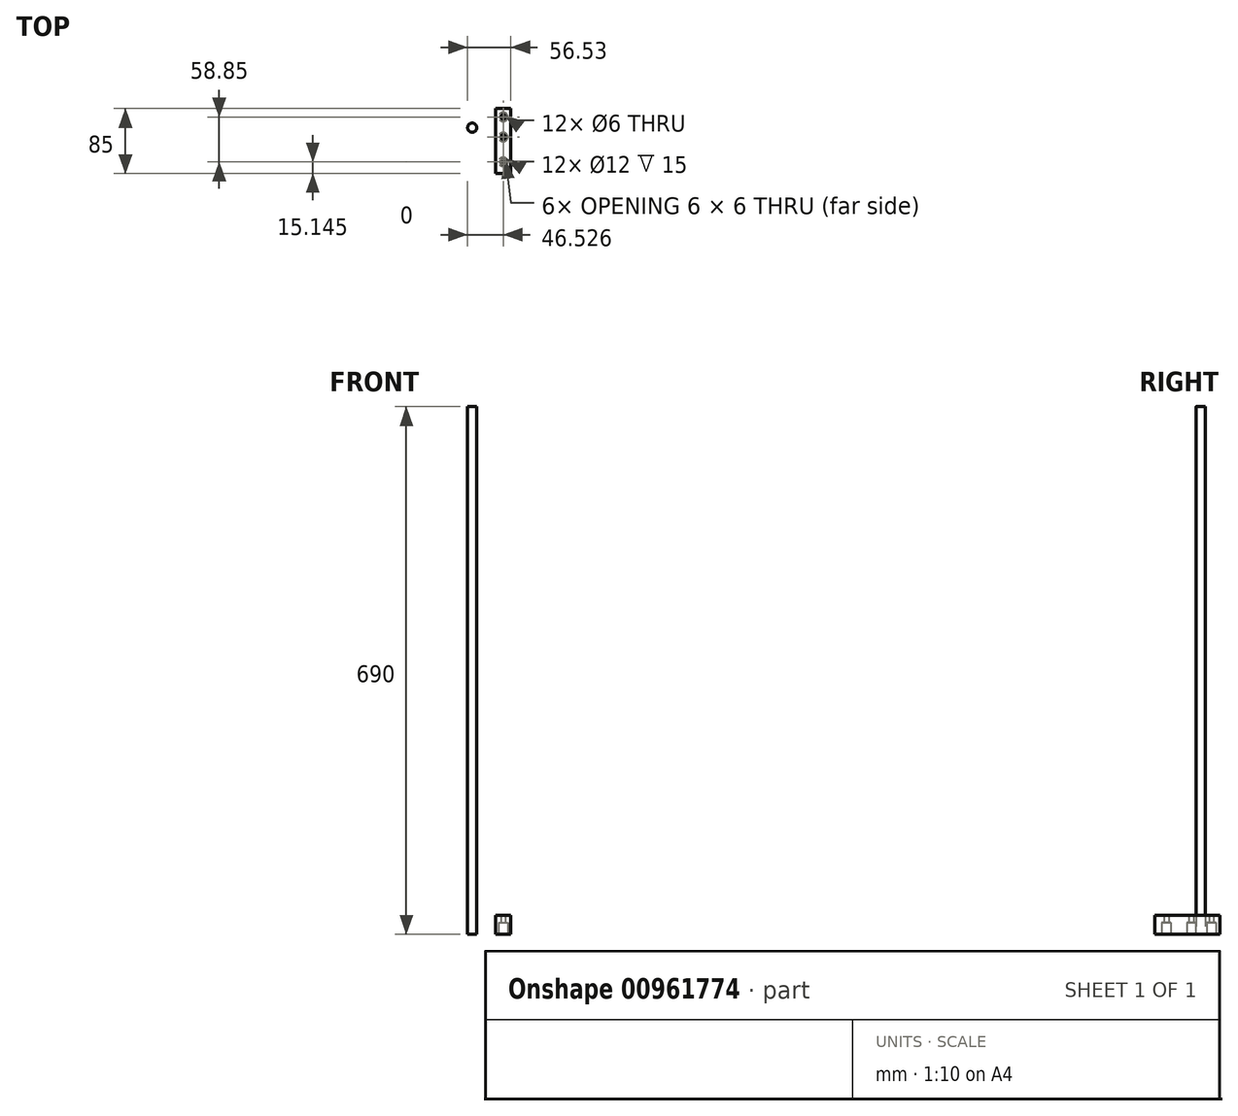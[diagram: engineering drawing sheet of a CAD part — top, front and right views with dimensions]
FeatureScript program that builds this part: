
annotation { "Feature Type Name" : "Feature", "Feature Type Description" : "" }
export const myFeature = defineFeature(function(context is Context, id is Id, definition is map)
    precondition{}
    {
        {
            var Q0;
            Q0=qCreatedBy(makeId("Top.planeOp"),FACE);
            var sketch = newSketch(context, id + "F0", { "sketchPlane" : qUnion([Q0])});
            skCircle(sketch, "E0", {"center": v(-96.13, 38.54) * mm, "radius": 6 * mm});
            skSolve(sketch);
        }
        {
            var Q0;
            Q0=makeQuery(id+"F0.imprint","IMPRINT",FACE,{"disambiguationData":[TD([[makeQuery(id+"F0.imprint","IMPRINT",EDGE,{"derivedFrom":sQuery(id+"F0.wireOp",EDGE,"E0")}),1.0]])]});
            extrude(context, id + "F1", {"entities" : qUnion([Q0]), "depth" : 690 * mm, "offsetDistance" : 25 * mm});
        }
        {
            var Q0;
            Q0=qCreatedBy(makeId("Top.planeOp"),FACE);
            var sketch = newSketch(context, id + "F2", { "sketchPlane" : qUnion([Q0])});
            skLineSegment(sketch, "E1.bottom", {"start": v(-65.6, 63.65) * mm, "end": v(-45.6, 63.65) * mm});
            skLineSegment(sketch, "E1.top", {"start": v(-65.6, -21.35) * mm, "end": v(-45.6, -21.35) * mm});
            skLineSegment(sketch, "E1.left", {"start": v(-65.6, 63.65) * mm, "end": v(-65.6, -21.35) * mm});
            skLineSegment(sketch, "E1.right", {"start": v(-45.6, 63.65) * mm, "end": v(-45.6, -21.35) * mm});
            skLineSegment(sketch, "E2", {"start": v(-55.6, -21.35) * mm, "end": v(-55.6, 63.65) * mm, "construction": true});
            skCircle(sketch, "E3", {"center": v(-55.6, -6.2) * mm, "radius": 2.5 * mm});
            skCircle(sketch, "E4.0.1.0", {"center": v(-55.6, 26.3) * mm, "radius": 2.5 * mm});
            skLineSegment(sketch, "E4.direction1", {"start": v(-55.6, -6.2) * mm, "end": v(-30.6, -6.2) * mm, "construction": true});
            skLineSegment(sketch, "E4.direction2", {"start": v(-55.6, -6.2) * mm, "end": v(-55.6, 26.3) * mm, "construction": true});
            skCircle(sketch, "E5", {"center": v(-55.6, 52.65) * mm, "radius": 6 * mm});
            skSolve(sketch);
        }
        {
            var Q0;
            Q0=makeQuery(id+"F2.imprint","IMPRINT",FACE,{"disambiguationData":[TD([[makeQuery(id+"F2.imprint","IMPRINT",EDGE,{"derivedFrom":sQuery(id+"F2.wireOp",EDGE,"E1.bottom")}),-1.0]])]});
            var Q1;
            Q1=makeQuery(id+"F2.imprint","IMPRINT",FACE,{"disambiguationData":[TD([[makeQuery(id+"F2.imprint","IMPRINT",EDGE,{"derivedFrom":sQuery(id+"F2.wireOp",EDGE,"E3")}),1.0]])]});
            var Q2;
            Q2=makeQuery(id+"F2.imprint","IMPRINT",FACE,{"disambiguationData":[TD([[makeQuery(id+"F2.imprint","IMPRINT",EDGE,{"derivedFrom":sQuery(id+"F2.wireOp",EDGE,"E4.0.1.0")}),1.0]])]});
            var Q3;
            Q3=makeQuery(id+"F2.imprint","IMPRINT",FACE,{"disambiguationData":[TD([[makeQuery(id+"F2.imprint","IMPRINT",EDGE,{"derivedFrom":sQuery(id+"F2.wireOp",EDGE,"E5")}),1.0]])]});
            extrude(context, id + "F3", {"entities" : qUnion([Q0, Q1, Q2, Q3]), "depth" : 25 * mm, "offsetDistance" : 25 * mm});
        }
        {
            var Q0;
            Q0=sQuery(id+"F2.wireOp",VERTEX,"E4.direction2.end");
            var Q1;
            Q1=sQuery(id+"F2.wireOp",VERTEX,"E4.direction1.start");
            var Q2;
            Q2=sQuery(id+"F2.wireOp",VERTEX,"E5.center");
            var Q3;
            Q3=makeQuery(id+"F3.opExtrude","SWEPT_BODY",BODY,{"disambiguationData":[OSD([sQuery(id+"F2.wireOp",EDGE,"E1.bottom"),sQuery(id+"F2.wireOp",EDGE,"E1.top"),sQuery(id+"F2.wireOp",EDGE,"E1.left"),sQuery(id+"F2.wireOp",EDGE,"E1.right"),sQuery(id+"F2.wireOp",EDGE,"E5")])]});
            hole(context, id + "F4", {"style" : HoleStyle.C_BORE, "endStyle" : HoleEndStyle.THROUGH, "oppositeDirection" : true, "holeDiameter" : 6 * mm, "cBoreDiameter" : 12 * mm, "cBoreDepth" : 15 * mm, "majorDiameter" : 5 * mm, "isTappedThrough" : true, "tappedDepth" : 12 * mm, "tapClearance" : 3, "locations" : qUnion([Q0, Q1, Q2]), "scope" : qUnion([Q3])});
        }
    });
